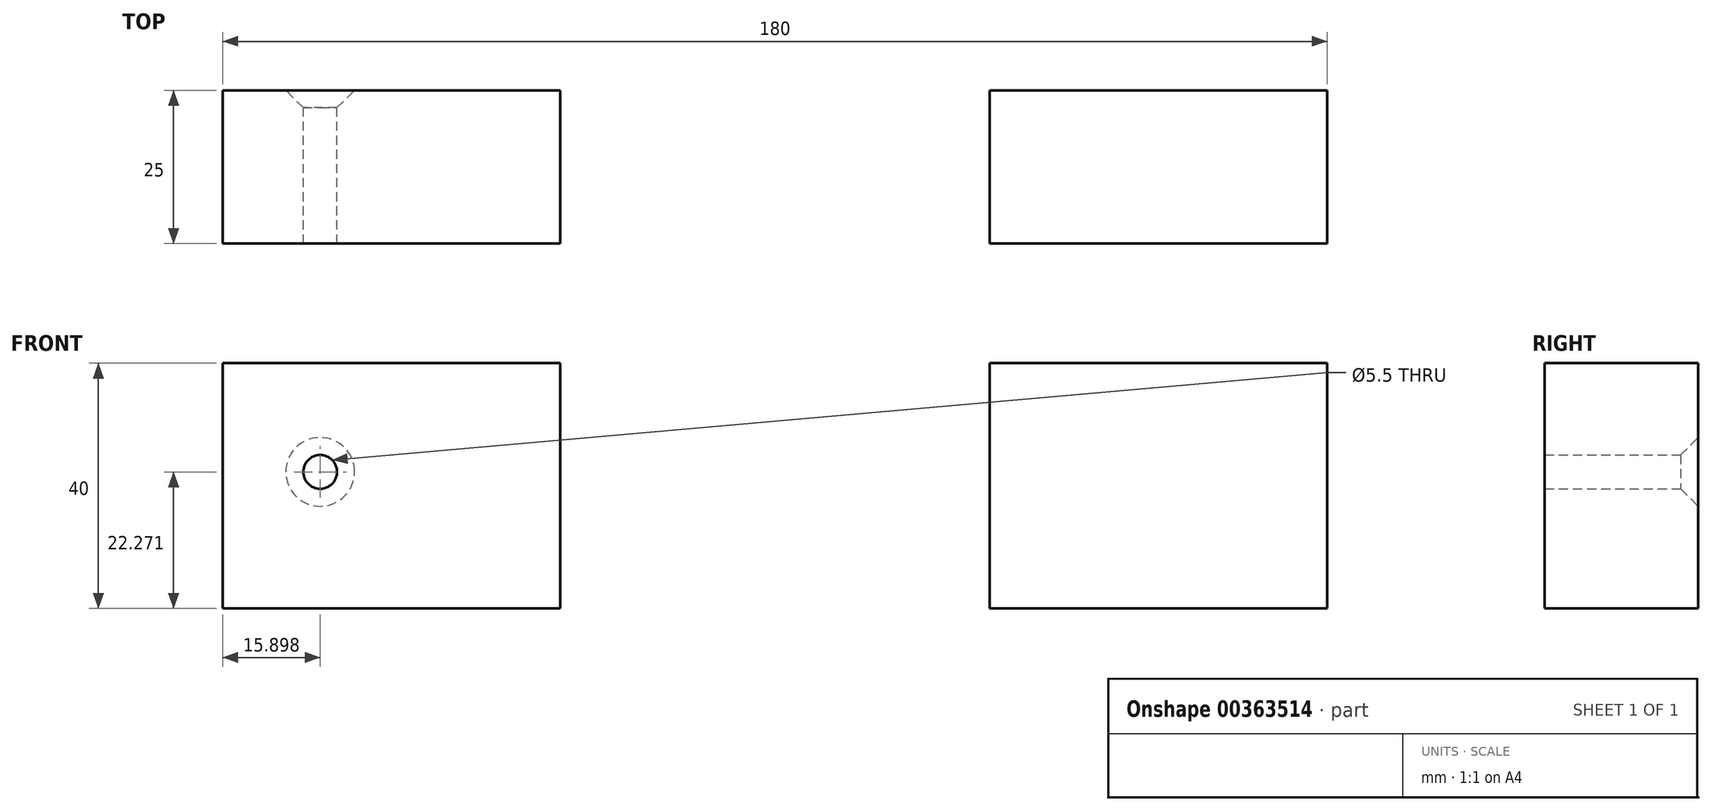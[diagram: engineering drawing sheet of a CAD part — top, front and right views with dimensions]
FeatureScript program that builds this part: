
annotation { "Feature Type Name" : "Feature", "Feature Type Description" : "" }
export const myFeature = defineFeature(function(context is Context, id is Id, definition is map)
    precondition{}
    {
        {
            var Q0;
            Q0=qCreatedBy(makeId("Front.planeOp"),FACE);
            var sketch = newSketch(context, id + "F0", { "sketchPlane" : qUnion([Q0])});
            skLineSegment(sketch, "E0.bottom", {"start": v(-110, -20) * mm, "end": v(110, -20) * mm});
            skLineSegment(sketch, "E0.top", {"start": v(-110, 20) * mm, "end": v(110, 20) * mm});
            skLineSegment(sketch, "E0.left", {"start": v(-110, -20) * mm, "end": v(-110, 20) * mm});
            skLineSegment(sketch, "E0.right", {"start": v(110, -20) * mm, "end": v(110, 20) * mm});
            skPoint(sketch, "E0.middle", {"position": v(0, 0) * mm});
            skLineSegment(sketch, "E1.0", {"start": v(90, -20) * mm, "end": v(90, 20) * mm});
            skLineSegment(sketch, "E2.0", {"start": v(-90, -20) * mm, "end": v(-90, 20) * mm});
            skLineSegment(sketch, "E3.bottom", {"start": v(-15, -20) * mm, "end": v(15, -20) * mm});
            skLineSegment(sketch, "E3.top", {"start": v(-15, 20) * mm, "end": v(15, 20) * mm});
            skLineSegment(sketch, "E3.left", {"start": v(-15, -20) * mm, "end": v(-15, 20) * mm});
            skLineSegment(sketch, "E3.right", {"start": v(15, -20) * mm, "end": v(15, 20) * mm});
            skLineSegment(sketch, "E4.0", {"start": v(-35, -20) * mm, "end": v(-35, 20) * mm});
            skLineSegment(sketch, "E5.0", {"start": v(35, -20) * mm, "end": v(35, 20) * mm});
            skPoint(sketch, "E6", {"position": v(-74.1, 2.27) * mm});
            skSolve(sketch);
        }
        {
            var Q0;
            {var subQ0=sQuery(id+"F0.wireOp",EDGE,"E2.0");Q0=makeQuery(id+"F0.imprint","IMPRINT",FACE,{"disambiguationData":[TD([[makeQuery(id+"F0.imprint","IMPRINT",EDGE,{"derivedFrom":subQ0}),-1.0]])]});}
            var Q1;
            {var subQ0=sQuery(id+"F0.wireOp",EDGE,"E1.0");Q1=makeQuery(id+"F0.imprint","IMPRINT",FACE,{"disambiguationData":[TD([[makeQuery(id+"F0.imprint","IMPRINT",EDGE,{"derivedFrom":subQ0}),1.0]])]});}
            extrude(context, id + "F1", {"entities" : qUnion([Q0, Q1]), "depth" : 25 * mm});
        }
        {
            var Q0;
            Q0=sQuery(id+"F0.wireOp",VERTEX,"E6");
            var Q1;
            Q1=makeQuery(id+"F1.opExtrude","SWEPT_BODY",BODY,{"disambiguationData":[OSD([sQuery(id+"F0.wireOp",EDGE,"E0.bottom"),sQuery(id+"F0.wireOp",EDGE,"E0.top"),sQuery(id+"F0.wireOp",EDGE,"E2.0"),sQuery(id+"F0.wireOp",EDGE,"E4.0")])]});
            hole(context, id + "F2", {"style" : HoleStyle.C_SINK, "endStyle" : HoleEndStyle.THROUGH, "oppositeDirection" : true, "standardTappedOrClearance" : lookupTablePath({ "standard" : "ISO", "fit" : "Normal", "size" : "M5", "type" : "Clearance" }), "standardBlindInLast" : lookupTablePath({ "fit" : "Standard", "standard" : "ISO", "size" : "M5", "type" : "Clearance" }), "holeDiameter" : 5.5 * mm, "cSinkDiameter" : 11.2 * mm, "cSinkAngle" : 90 * degree, "isTappedThrough" : true, "tappedDepth" : 12 * mm, "tapClearance" : 3, "locations" : qUnion([Q0]), "scope" : qUnion([Q1])});
        }
    });
